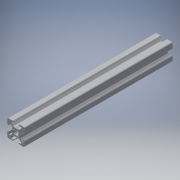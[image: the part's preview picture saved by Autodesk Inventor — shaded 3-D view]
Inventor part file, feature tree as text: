
AUTODESK INVENTOR PART (.ipt)
format: ipt  version: 2019 (Build 230136000, 136)  size: 311,808 bytes
history: native  units: in
note: dims shown in document units (in); Inventor stores cm internally (conversion verified against a paired STEP export)
features: other x3, extrude x1, sketch x1
ambient origin geometry x8: Origin, YZ Plane, XZ Plane, XY Plane, X Axis, Y Axis, Z Axis, Center Point
bodies: Solid1 (feature_tree)
feature tree (5):
  other  "Blocks"
  extrude  "Extrusion1"  Depth=1.0in
  sketch  "Sketch1"  dims[d1=0.0in d13=1.0in d14=1.0in]
  other  "20x20"
  other  "20x20:1"
